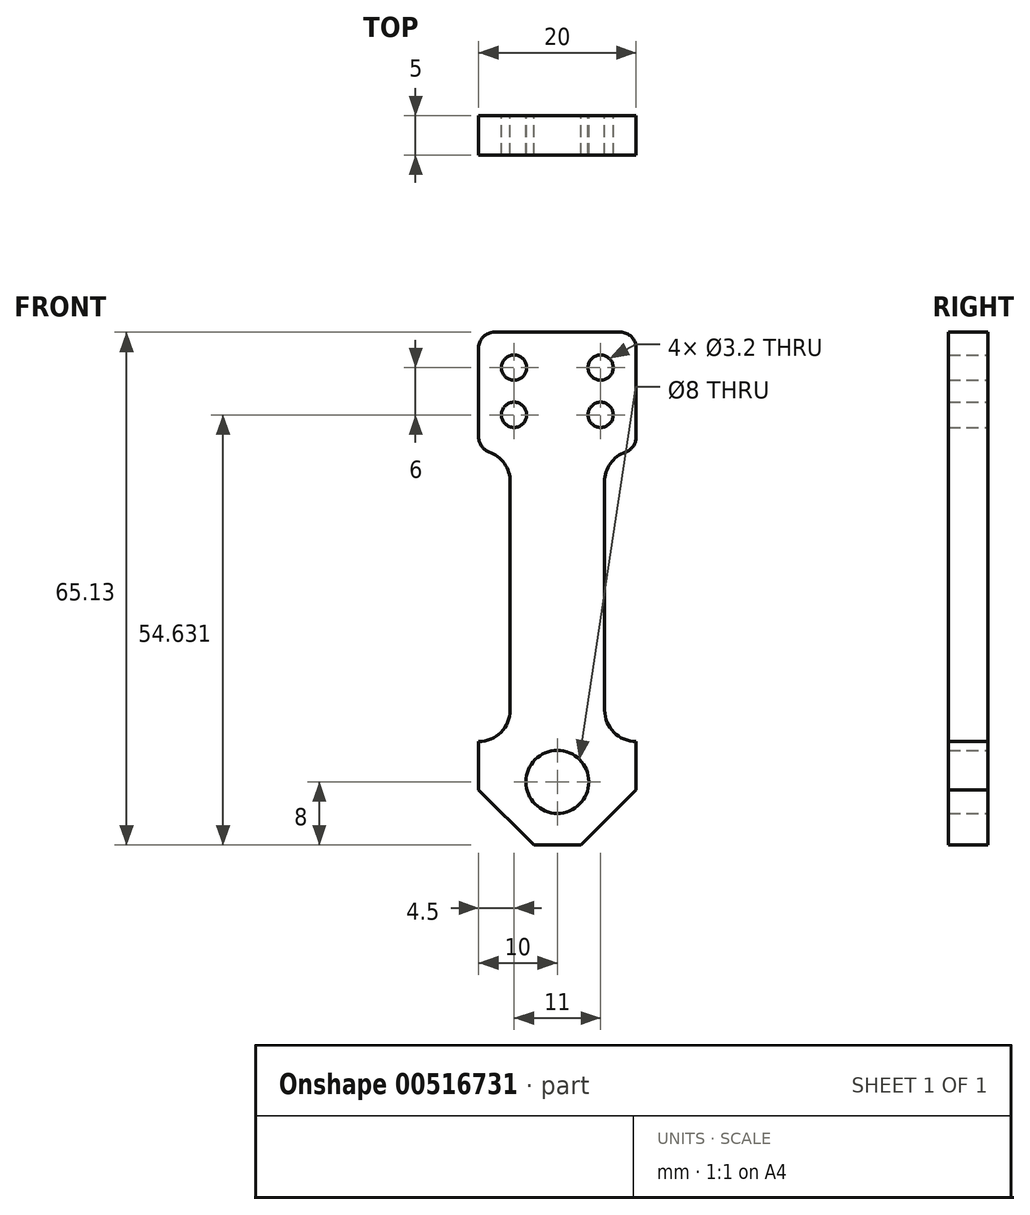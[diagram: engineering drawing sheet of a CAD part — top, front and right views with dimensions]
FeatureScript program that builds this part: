
annotation { "Feature Type Name" : "Feature", "Feature Type Description" : "" }
export const myFeature = defineFeature(function(context is Context, id is Id, definition is map)
    precondition{}
    {
        {
            var Q0;
            Q0=qCreatedBy(makeId("Front.planeOp"),FACE);
            var sketch = newSketch(context, id + "F0", { "sketchPlane" : qUnion([Q0])});
            skCircle(sketch, "E0", {"center": v(0, 0) * mm, "radius": 4 * mm});
            skLineSegment(sketch, "E1.bottom", {"start": v(-10, 57.13) * mm, "end": v(10, 57.13) * mm});
            skLineSegment(sketch, "E1.top", {"start": v(-3, -8) * mm, "end": v(3, -8) * mm});
            skLineSegment(sketch, "E1.left", {"start": v(-10, 57.13) * mm, "end": v(-10, 42.13) * mm});
            skLineSegment(sketch, "E1.right", {"start": v(10, 57.13) * mm, "end": v(10, 42.13) * mm});
            skLineSegment(sketch, "E2", {"start": v(-3, -8) * mm, "end": v(-10, -1) * mm});
            skLineSegment(sketch, "E3", {"start": v(10, -1) * mm, "end": v(3, -8) * mm});
            skLineSegment(sketch, "E4", {"start": v(6, 38.13) * mm, "end": v(6, 9.13) * mm});
            skArc(sketch, "E5", {"start": v(6, 38.13) * mm, "mid": v(7.17, 40.96) * mm, "end": v(10, 42.13) * mm});
            skArc(sketch, "E6", {"start": v(6, 9.13) * mm, "mid": v(7.17, 6.3) * mm, "end": v(10, 5.13) * mm});
            skArc(sketch, "E7.MirrorCS", {"start": v(-6, 9.13) * mm, "mid": v(-7.17, 6.3) * mm, "end": v(-10, 5.13) * mm});
            skLineSegment(sketch, "E8.MirrorCS", {"start": v(-6, 38.13) * mm, "end": v(-6, 9.13) * mm});
            skArc(sketch, "E9.MirrorCS", {"start": v(-6, 38.13) * mm, "mid": v(-7.17, 40.96) * mm, "end": v(-10, 42.13) * mm});
            skLineSegment(sketch, "E10.trimOffspring", {"start": v(-10, 5.13) * mm, "end": v(-10, -1) * mm});
            skLineSegment(sketch, "E11.trimOffspring", {"start": v(10, 5.13) * mm, "end": v(10, -1) * mm});
            skCircle(sketch, "E12", {"center": v(-5.5, 52.63) * mm, "radius": 1.6 * mm});
            skCircle(sketch, "E13", {"center": v(-5.5, 46.63) * mm, "radius": 1.6 * mm});
            skCircle(sketch, "E14.MirrorC", {"center": v(5.5, 52.63) * mm, "radius": 1.6 * mm});
            skCircle(sketch, "E15.MirrorC", {"center": v(5.5, 46.63) * mm, "radius": 1.6 * mm});
            skSolve(sketch);
        }
        {
            var Q0;
            Q0 = qSketchRegion(id + "F0", true);
            extrude(context, id + "F1", {"entities" : qUnion([Q0]), "depth" : 5 * mm, "offsetDistance" : 25 * mm});
        }
        {
            var Q0;
            Q0=makeQuery(id+"F1.opExtrude","SWEPT_EDGE",EDGE,{"disambiguationData":[OSD([sQuery(id+"F0.wireOp",EDGE,"E1.bottom"),sQuery(id+"F0.wireOp",EDGE,"E1.right")])]});
            var Q1;
            Q1=makeQuery(id+"F1.opExtrude","SWEPT_EDGE",EDGE,{"disambiguationData":[OSD([sQuery(id+"F0.wireOp",EDGE,"E1.right"),sQuery(id+"F0.wireOp",EDGE,"E5")])]});
            var Q2;
            Q2=makeQuery(id+"F1.opExtrude","SWEPT_EDGE",EDGE,{"disambiguationData":[OSD([sQuery(id+"F0.wireOp",EDGE,"E1.left"),sQuery(id+"F0.wireOp",EDGE,"E9.MirrorCS")])]});
            var Q3;
            Q3=makeQuery(id+"F1.opExtrude","SWEPT_EDGE",EDGE,{"disambiguationData":[OSD([sQuery(id+"F0.wireOp",EDGE,"E1.bottom"),sQuery(id+"F0.wireOp",EDGE,"E1.left")])]});
            fillet(context, id + "F2", {"entities" : qUnion([Q0, Q1, Q2, Q3]), "radius" : 2 * mm, "tangentPropagation" : true, "allowEdgeOverflow" : false});
        }
    });
